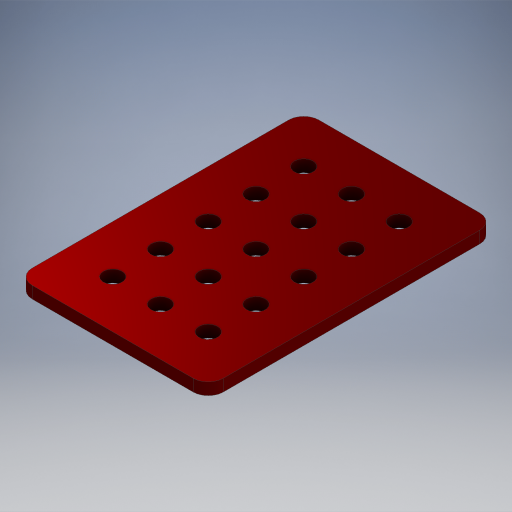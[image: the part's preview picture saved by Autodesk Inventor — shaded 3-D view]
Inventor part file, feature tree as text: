
AUTODESK INVENTOR PART (.ipt)
format: ipt  version: 2024.2 (Build 282272000, 272)  size: 299,520 bytes
history: native  units: in
note: dims shown in document units (in); Inventor stores cm internally (conversion verified against a paired STEP export)
features: extrude x1, sketch x1
ambient origin geometry x8: Origin, YZ Plane, XZ Plane, XY Plane, X Axis, Y Axis, Z Axis, Center Point
bodies: Solid1 (feature_tree)
feature tree (2):
  extrude  "Extrusion1"  Depth=0.125in
  sketch  "Sketch1"  dims[d0=0.196in d1=0.196in d2=0.5in d3=0.196in d4=0.5in d5=1.9685in d7=0.5in d8=0.3937in d10=1.0in d14=2.0in d15=3.0in d16=0.157in d17=0.125in d18=0.0in]
